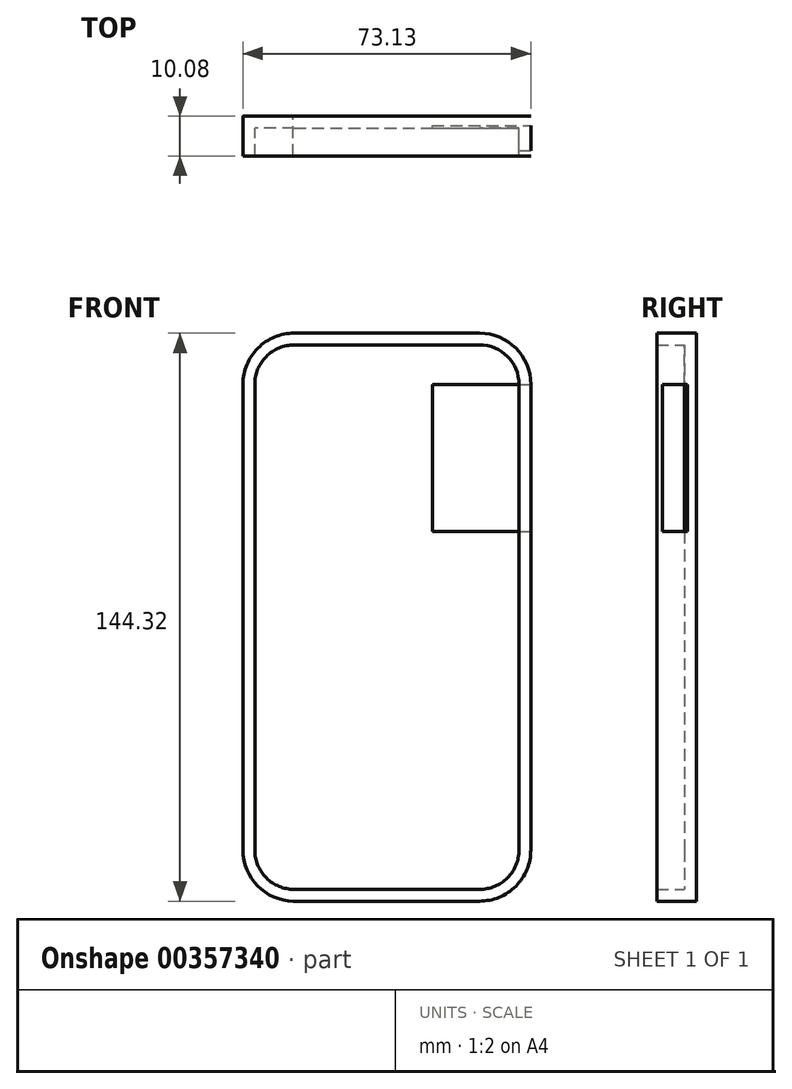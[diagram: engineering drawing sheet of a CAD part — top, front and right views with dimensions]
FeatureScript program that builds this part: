
annotation { "Feature Type Name" : "Feature", "Feature Type Description" : "" }
export const myFeature = defineFeature(function(context is Context, id is Id, definition is map)
    precondition{}
    {
        {
            var Q0;
            Q0=qCreatedBy(makeId("Front.planeOp"),FACE);
            var sketch = newSketch(context, id + "F0", { "sketchPlane" : qUnion([Q0])});
            skLineSegment(sketch, "E0.bottom", {"start": v(-23.56, 69.16) * mm, "end": v(23.57, 69.16) * mm});
            skLineSegment(sketch, "E0.top", {"start": v(-23.56, -69.16) * mm, "end": v(23.56, -69.16) * mm});
            skLineSegment(sketch, "E0.left", {"start": v(-33.56, 59.16) * mm, "end": v(-33.56, -59.16) * mm});
            skLineSegment(sketch, "E0.right", {"start": v(33.57, 59.16) * mm, "end": v(33.56, -59.16) * mm});
            skPoint(sketch, "E0.middle", {"position": v(0, 0) * mm});
            skLineSegment(sketch, "E1.bottom", {"start": v(-29.36, 51.58) * mm, "end": v(29.37, 51.58) * mm});
            skLineSegment(sketch, "E1.top", {"start": v(-29.37, -51.57) * mm, "end": v(29.36, -51.57) * mm});
            skLineSegment(sketch, "E1.left", {"start": v(-29.36, 51.58) * mm, "end": v(-29.37, -51.57) * mm});
            skLineSegment(sketch, "E1.right", {"start": v(29.37, 51.58) * mm, "end": v(29.36, -51.57) * mm});
            skCircle(sketch, "E2", {"center": v(0, -60.03) * mm, "radius": 4.7 * mm});
            skPoint(sketch, "E2.centerSnap0", {"position": v(0, -51.57) * mm});
            skPoint(sketch, "E3.visualSharp", {"position": v(-33.56, 69.16) * mm});
            skArc(sketch, "E3.filletArc", {"start": v(-23.56, 69.16) * mm, "mid": v(-30.64, 66.23) * mm, "end": v(-33.56, 59.16) * mm});
            skPoint(sketch, "E4.visualSharp", {"position": v(33.57, 69.16) * mm});
            skArc(sketch, "E4.filletArc", {"start": v(33.57, 59.16) * mm, "mid": v(30.64, 66.23) * mm, "end": v(23.57, 69.16) * mm});
            skPoint(sketch, "E5.visualSharp", {"position": v(33.56, -69.16) * mm});
            skArc(sketch, "E5.filletArc", {"start": v(23.56, -69.16) * mm, "mid": v(30.64, -66.23) * mm, "end": v(33.56, -59.16) * mm});
            skPoint(sketch, "E6.visualSharp", {"position": v(-33.56, -69.16) * mm});
            skArc(sketch, "E6.filletArc", {"start": v(-33.56, -59.16) * mm, "mid": v(-30.64, -66.23) * mm, "end": v(-23.56, -69.16) * mm});
            skCircle(sketch, "E7", {"center": v(21.34, 59.16) * mm, "radius": 5.35 * mm});
            skCircle(sketch, "E8", {"center": v(10.27, 59.16) * mm, "radius": 2.2 * mm});
            skCircle(sketch, "E9", {"center": v(14.3, 59.15) * mm, "radius": 1.06 * mm});
            skSolve(sketch);
        }
        {
            var Q0;
            Q0=makeQuery(id+"F0.imprint","IMPRINT",FACE,{"disambiguationData":[TD([[makeQuery(id+"F0.imprint","IMPRINT",EDGE,{"derivedFrom":sQuery(id+"F0.wireOp",EDGE,"E0.bottom")}),-1.0]])]});
            var Q1;
            Q1=makeQuery(id+"F0.imprint","IMPRINT",FACE,{"disambiguationData":[TD([[makeQuery(id+"F0.imprint","IMPRINT",EDGE,{"derivedFrom":sQuery(id+"F0.wireOp",EDGE,"E1.bottom")}),-1.0]])]});
            var Q2;
            Q2=makeQuery(id+"F0.imprint","IMPRINT",FACE,{"disambiguationData":[TD([[makeQuery(id+"F0.imprint","IMPRINT",EDGE,{"derivedFrom":sQuery(id+"F0.wireOp",EDGE,"E7")}),1.0]])]});
            var Q3;
            Q3=makeQuery(id+"F0.imprint","IMPRINT",FACE,{"disambiguationData":[TD([[makeQuery(id+"F0.imprint","IMPRINT",EDGE,{"derivedFrom":sQuery(id+"F0.wireOp",EDGE,"E2")}),1.0]])]});
            var Q4;
            Q4=makeQuery(id+"F0.imprint","IMPRINT",FACE,{"disambiguationData":[TD([[makeQuery(id+"F0.imprint","IMPRINT",EDGE,{"derivedFrom":sQuery(id+"F0.wireOp",EDGE,"E8")}),1.0]])]});
            var Q5;
            Q5=makeQuery(id+"F0.imprint","IMPRINT",FACE,{"disambiguationData":[TD([[makeQuery(id+"F0.imprint","IMPRINT",EDGE,{"derivedFrom":sQuery(id+"F0.wireOp",EDGE,"E9")}),1.0]])]});
            extrude(context, id + "F1", {"entities" : qUnion([Q0, Q1, Q2, Q3, Q4, Q5]), "depth" : 7.08 * mm});
        }
        {
            var Q0;
            Q0=makeQuery(id+"F0.imprint","IMPRINT",FACE,{"disambiguationData":[TD([[makeQuery(id+"F0.imprint","IMPRINT",EDGE,{"derivedFrom":sQuery(id+"F0.wireOp",EDGE,"E1.bottom")}),-1.0]])]});
            var Q1;
            Q1=makeQuery(id+"F0.imprint","IMPRINT",FACE,{"disambiguationData":[TD([[makeQuery(id+"F0.imprint","IMPRINT",EDGE,{"derivedFrom":sQuery(id+"F0.wireOp",EDGE,"E2")}),1.0]])]});
            extrude(context, id + "F2", {"entities" : qUnion([Q0, Q1]), "operationType" : NewBodyOperationType.ADD, "depth" : 7.08 * mm});
        }
        {
            var Q0;
            Q0=makeQuery(id+"F1.opExtrude","SWEPT_FACE",FACE,{"disambiguationData":[OSD([sQuery(id+"F0.wireOp",EDGE,"E0.left")])]});
            var sketch = newSketch(context, id + "F3", { "sketchPlane" : qUnion([Q0])});
            skLineSegment(sketch, "E10.bottom", {"start": v(4.08, 37.72) * mm, "end": v(3, 37.72) * mm});
            skLineSegment(sketch, "E10.top", {"start": v(4.08, 49.89) * mm, "end": v(3, 49.89) * mm});
            skLineSegment(sketch, "E10.left", {"start": v(5.18, 38.82) * mm, "end": v(5.18, 48.79) * mm});
            skLineSegment(sketch, "E10.right", {"start": v(1.9, 38.82) * mm, "end": v(1.9, 48.79) * mm});
            skPoint(sketch, "E10.middle", {"position": v(3.54, 43.8) * mm});
            skPoint(sketch, "E11.visualSharp", {"position": v(5.18, 49.89) * mm});
            skArc(sketch, "E11.filletArc", {"start": v(5.18, 48.79) * mm, "mid": v(4.85, 49.57) * mm, "end": v(4.08, 49.89) * mm});
            skPoint(sketch, "E12.visualSharp", {"position": v(1.9, 49.89) * mm});
            skArc(sketch, "E12.filletArc", {"start": v(3, 49.89) * mm, "mid": v(2.23, 49.57) * mm, "end": v(1.9, 48.79) * mm});
            skPoint(sketch, "E13.visualSharp", {"position": v(5.18, 37.72) * mm});
            skArc(sketch, "E13.filletArc", {"start": v(4.08, 37.72) * mm, "mid": v(4.85, 38.04) * mm, "end": v(5.18, 38.82) * mm});
            skPoint(sketch, "E14.visualSharp", {"position": v(1.9, 37.72) * mm});
            skArc(sketch, "E14.filletArc", {"start": v(1.9, 38.82) * mm, "mid": v(2.23, 38.04) * mm, "end": v(3, 37.72) * mm});
            skLineSegment(sketch, "E15.bottom", {"start": v(4.66, 53.95) * mm, "end": v(2.73, 53.95) * mm});
            skLineSegment(sketch, "E15.top", {"start": v(4.56, 56.83) * mm, "end": v(2.63, 56.83) * mm});
            skLineSegment(sketch, "E15.left", {"start": v(5.66, 54.95) * mm, "end": v(5.66, 55.73) * mm});
            skLineSegment(sketch, "E15.right", {"start": v(1.63, 55.05) * mm, "end": v(1.63, 55.83) * mm});
            skPoint(sketch, "E15.middle", {"position": v(3.64, 55.39) * mm});
            skLineSegment(sketch, "E16.bottom", {"start": v(3.98, 23.74) * mm, "end": v(2.71, 23.74) * mm});
            skLineSegment(sketch, "E16.top", {"start": v(3.97, 33.7) * mm, "end": v(2.7, 33.7) * mm});
            skLineSegment(sketch, "E16.left", {"start": v(4.98, 24.74) * mm, "end": v(4.97, 32.7) * mm});
            skLineSegment(sketch, "E16.right", {"start": v(1.71, 24.74) * mm, "end": v(1.7, 32.7) * mm});
            skPoint(sketch, "E16.middle", {"position": v(3.34, 28.72) * mm});
            skPoint(sketch, "E17.visualSharp", {"position": v(4.97, 33.7) * mm});
            skArc(sketch, "E17.filletArc", {"start": v(4.97, 32.7) * mm, "mid": v(4.68, 33.41) * mm, "end": v(3.97, 33.7) * mm});
            skPoint(sketch, "E18.visualSharp", {"position": v(1.7, 33.7) * mm});
            skArc(sketch, "E18.filletArc", {"start": v(2.7, 33.7) * mm, "mid": v(2, 33.41) * mm, "end": v(1.7, 32.7) * mm});
            skPoint(sketch, "E19.visualSharp", {"position": v(4.98, 23.74) * mm});
            skArc(sketch, "E19.filletArc", {"start": v(3.98, 23.74) * mm, "mid": v(4.68, 24.03) * mm, "end": v(4.98, 24.74) * mm});
            skPoint(sketch, "E20.visualSharp", {"position": v(1.71, 23.74) * mm});
            skArc(sketch, "E20.filletArc", {"start": v(1.71, 24.74) * mm, "mid": v(2, 24.03) * mm, "end": v(2.71, 23.74) * mm});
            skPoint(sketch, "E21.visualSharp", {"position": v(5.66, 56.83) * mm});
            skArc(sketch, "E21.filletArc", {"start": v(5.66, 55.73) * mm, "mid": v(5.34, 56.5) * mm, "end": v(4.56, 56.83) * mm});
            skPoint(sketch, "E22.visualSharp", {"position": v(5.66, 53.95) * mm});
            skArc(sketch, "E22.filletArc", {"start": v(4.66, 53.95) * mm, "mid": v(5.36, 54.24) * mm, "end": v(5.66, 54.95) * mm});
            skPoint(sketch, "E23.visualSharp", {"position": v(1.63, 53.95) * mm});
            skArc(sketch, "E23.filletArc", {"start": v(1.63, 55.05) * mm, "mid": v(1.95, 54.27) * mm, "end": v(2.73, 53.95) * mm});
            skPoint(sketch, "E24.visualSharp", {"position": v(1.63, 56.83) * mm});
            skArc(sketch, "E24.filletArc", {"start": v(2.63, 56.83) * mm, "mid": v(1.92, 56.53) * mm, "end": v(1.63, 55.83) * mm});
            skSolve(sketch);
        }
        {
            var Q0;
            Q0=makeQuery(id+"F0.imprint","IMPRINT",FACE,{"disambiguationData":[TD([[makeQuery(id+"F0.imprint","IMPRINT",EDGE,{"derivedFrom":sQuery(id+"F0.wireOp",EDGE,"E7")}),1.0]])]});
            extrude(context, id + "F4", {"entities" : qUnion([Q0]), "operationType" : NewBodyOperationType.ADD, "depth" : 0.8 * mm});
        }
        {
            var Q0;
            Q0=makeQuery(id+"F1.opExtrude","CAP_FACE",FACE,{"disambiguationData":[OSD([sQuery(id+"F0.wireOp",EDGE,"E0.bottom"),sQuery(id+"F0.wireOp",EDGE,"E0.top"),sQuery(id+"F0.wireOp",EDGE,"E0.left"),sQuery(id+"F0.wireOp",EDGE,"E0.right"),sQuery(id+"F0.wireOp",EDGE,"E3.filletArc"),sQuery(id+"F0.wireOp",EDGE,"E4.filletArc"),sQuery(id+"F0.wireOp",EDGE,"E5.filletArc"),sQuery(id+"F0.wireOp",EDGE,"E6.filletArc")])],"isStart":false});
            var Q1;
            Q1=makeQuery(id+"F1.opExtrude","SWEPT_BODY",BODY,{"disambiguationData":[OSD([sQuery(id+"F0.wireOp",EDGE,"E0.bottom"),sQuery(id+"F0.wireOp",EDGE,"E0.top"),sQuery(id+"F0.wireOp",EDGE,"E0.left"),sQuery(id+"F0.wireOp",EDGE,"E0.right"),sQuery(id+"F0.wireOp",EDGE,"E3.filletArc"),sQuery(id+"F0.wireOp",EDGE,"E4.filletArc"),sQuery(id+"F0.wireOp",EDGE,"E5.filletArc"),sQuery(id+"F0.wireOp",EDGE,"E6.filletArc")])]});
            shell(context, id + "F5", {"entities" : qUnion([Q0]), "parts" : qUnion([Q1]), "thickness" : 3 * mm, "oppositeDirection" : true});
        }
        {
            var Q0;
            Q0=makeQuery(id+"F1.opExtrude","SWEPT_FACE",FACE,{"disambiguationData":[OSD([sQuery(id+"F0.wireOp",EDGE,"E0.right")])]});
            var sketch = newSketch(context, id + "F6", { "sketchPlane" : qUnion([Q0])});
            skLineSegment(sketch, "E25.bottom", {"start": v(3, 0) * mm, "end": v(-3, 0) * mm});
            skLineSegment(sketch, "E25.top", {"start": v(3, -1.55) * mm, "end": v(-3, -1.55) * mm});
            skLineSegment(sketch, "E25.left", {"start": v(3, 0) * mm, "end": v(3, -1.55) * mm});
            skLineSegment(sketch, "E25.right", {"start": v(-3, 0) * mm, "end": v(-3, -1.55) * mm});
            skPoint(sketch, "E25.middle", {"position": v(0, -0.78) * mm});
            skLineSegment(sketch, "E26.bottom", {"start": v(-5.68, 21.73) * mm, "end": v(0.65, 21.73) * mm});
            skLineSegment(sketch, "E26.top", {"start": v(-5.68, 59.73) * mm, "end": v(0.65, 59.73) * mm});
            skLineSegment(sketch, "E26.left", {"start": v(-5.68, 21.73) * mm, "end": v(-5.68, 59.73) * mm});
            skLineSegment(sketch, "E26.right", {"start": v(0.65, 21.73) * mm, "end": v(0.65, 59.73) * mm});
            skPoint(sketch, "E26.middle", {"position": v(-2.52, 40.73) * mm});
            skSolve(sketch);
        }
        {
            var Q0;
            {var subQ0=sQuery(id+"F6.wireOp",EDGE,"E26.bottom");Q0=makeQuery(id+"F6.imprint","IMPRINT",FACE,{"disambiguationData":[TD([[makeQuery(id+"F6.imprint","IMPRINT",EDGE,{"derivedFrom":subQ0}),1.0]])]});}
            var Q1;
            Q1=makeQuery(id+"F1.opExtrude","SWEPT_FACE",FACE,{"disambiguationData":[OSD([sQuery(id+"F0.wireOp",EDGE,"E0.top")])]});
            extrude(context, id + "F7", {"entities" : qUnion([Q0, Q1]), "operationType" : NewBodyOperationType.REMOVE, "oppositeDirection" : true, "depth" : 25 * mm});
        }
    });
